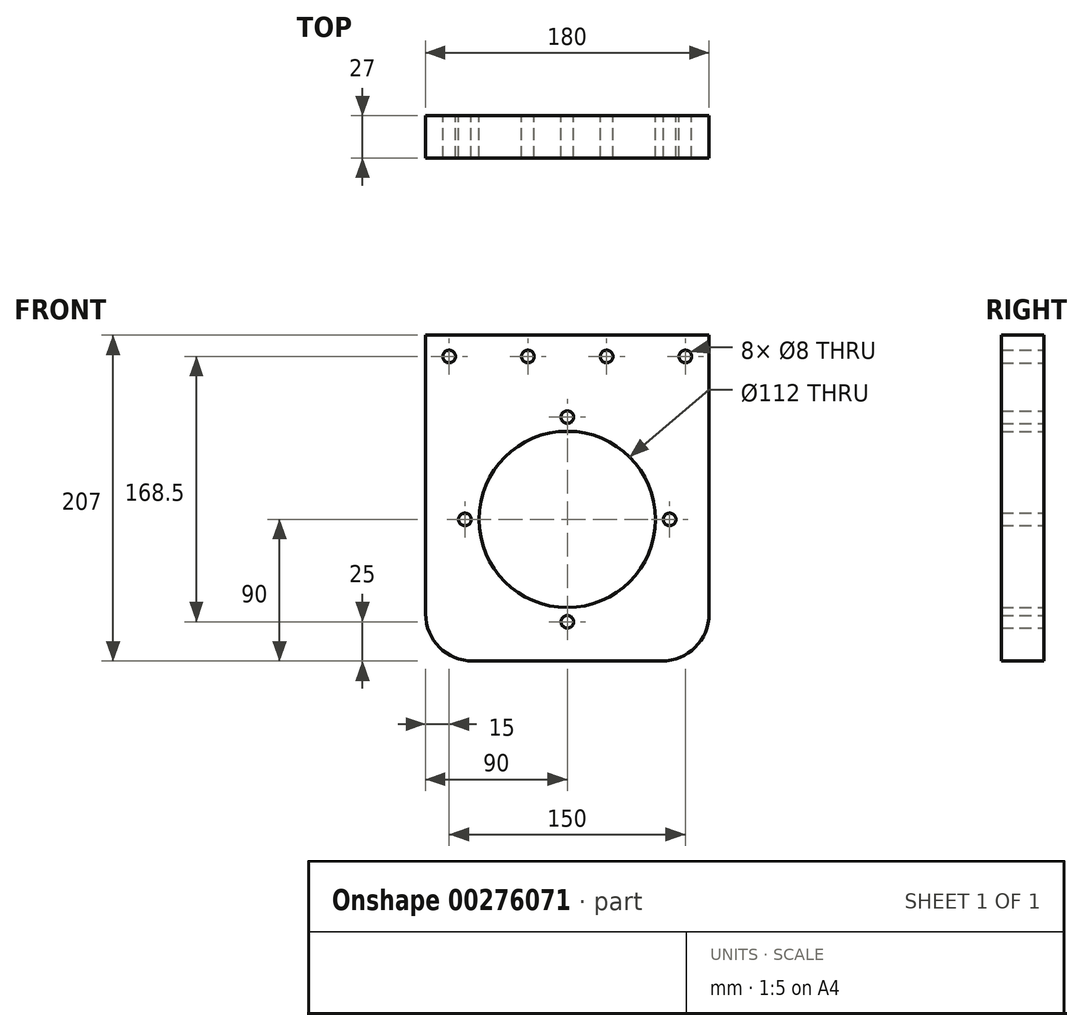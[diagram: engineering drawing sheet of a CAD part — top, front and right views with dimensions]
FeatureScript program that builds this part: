
annotation { "Feature Type Name" : "Feature", "Feature Type Description" : "" }
export const myFeature = defineFeature(function(context is Context, id is Id, definition is map)
    precondition{}
    {
        {
            var Q0;
            Q0=qCreatedBy(makeId("Front.planeOp"),FACE);
            var sketch = newSketch(context, id + "F0", { "sketchPlane" : qUnion([Q0])});
            skLineSegment(sketch, "E0.bottom", {"start": v(-60, -180) * mm, "end": v(60, -180) * mm});
            skLineSegment(sketch, "E0.top", {"start": v(-90, 27) * mm, "end": v(90, 27) * mm});
            skLineSegment(sketch, "E0.left", {"start": v(-90, -150) * mm, "end": v(-90, 27) * mm});
            skLineSegment(sketch, "E0.right", {"start": v(90, -150) * mm, "end": v(90, 27) * mm});
            skCircle(sketch, "E1", {"center": v(0, -90) * mm, "radius": 56 * mm});
            skCircle(sketch, "E2", {"center": v(65, -90) * mm, "radius": 4 * mm});
            skCircle(sketch, "E3", {"center": v(0, -25) * mm, "radius": 4 * mm});
            skCircle(sketch, "E4", {"center": v(-65, -90) * mm, "radius": 4 * mm});
            skCircle(sketch, "E5", {"center": v(0, -155) * mm, "radius": 4 * mm});
            skPoint(sketch, "E6.visualSharp", {"position": v(-90, -180) * mm});
            skArc(sketch, "E6.filletArc", {"start": v(-90, -150) * mm, "mid": v(-81.21, -171.21) * mm, "end": v(-60, -180) * mm});
            skPoint(sketch, "E7.visualSharp", {"position": v(90, -180) * mm});
            skArc(sketch, "E7.filletArc", {"start": v(60, -180) * mm, "mid": v(81.21, -171.21) * mm, "end": v(90, -150) * mm});
            skCircle(sketch, "E8", {"center": v(-75, 13.5) * mm, "radius": 4 * mm});
            skCircle(sketch, "E9", {"center": v(-25, 13.5) * mm, "radius": 4 * mm});
            skCircle(sketch, "E10", {"center": v(25, 13.5) * mm, "radius": 4 * mm});
            skCircle(sketch, "E11", {"center": v(75, 13.5) * mm, "radius": 4 * mm});
            skLineSegment(sketch, "E12", {"start": v(-75, 13.5) * mm, "end": v(75, 13.5) * mm, "construction": true});
            skSolve(sketch);
        }
        {
            var Q0;
            Q0=makeQuery(id+"F0.imprint","IMPRINT",FACE,{"disambiguationData":[TD([[makeQuery(id+"F0.imprint","IMPRINT",EDGE,{"derivedFrom":sQuery(id+"F0.wireOp",EDGE,"E0.bottom")}),1.0]])]});
            extrude(context, id + "F1", {"entities" : qUnion([Q0]), "endBound" : BoundingType.SYMMETRIC, "depth" : 27 * mm});
        }
    });
